# Revit family: Grinder_Pump-Dual_Seal-Zoeller-7011
name_source: partatom
category: Mechanical Equipment
units: mm (PartAtom-declared; Revit-internal decimal feet)

## family parameters
Always vertical = No
Cut with Voids When Loaded = No
OmniClass Number = 23.60.30.21
OmniClass Title = Pumps
Part Type = Normal
Room Calculation Point = No
Round Connector Dimension = Use Radius
Shared = Yes
Work Plane-Based = Yes

## types (1)
- 7011
    Assembly Code = D2010900
    Configuration = Reversing
    Cutter & Plate SS Hardened = 55-60 Rockwell
    Default Elevation = 0"
    Description = Commercial Effluent Pumps
    Discharge Diameter = 1.25" NPT
    Discharge Radius = 5/8"
    Full Load Amps (Voltage Dependent) = 4.5-20.0
    Height = 21 3/32"
    Hertz = 60
    Impeller Diameter = 5 17/32"
    Impeller Trim - Reversing Models Only (Optional) = No
    Impeller Type = Ductile Iron Vortex
    Installation Type = Floor Mounted
    Insulation = Class F
    Lead Wires Insulation = Class F
    Length = 11 19/32"
    Locked Rotor Amps (Voltage Dependant) = 16.2-60.7
    Manufacturer = Zoeller
    Masterformat Number = 33 36 16
    Masterformat Title = Utility Septic Tank Effluent Pumps
    Material = Cast Iron-Zoeller-Powder Coated Epoxy
    Max. Stator Temp. = 311 °F
    Max. Water Temp. = 104 °F
    Maximum KW Input = 3.9
    Model = 7011
    Moisture Sensor (Optional) = Moisture Sensing Probes (Requires a circuit in control panel)
    Motor = 2.0 Pump Name Plate Horsepower
    Motor Design Letter = NEMA B (3 Ph), NEMA L (1 Ph)
    Motor Shaft = 416 S.S.
    Motor Thermal Shutoff = Integral On-Lead (1 PH) or Thermal Cut-Out (3 PH)
    Motor Type = Submersible
    NEC Locked Rotor Code = K
    Nominal Height = 5 3/8"
    O-Rings = Viton
    Omniclass Table 23 Code = 23.60.30.21
    Omniclass Table 23 Title = Pumps
    Operation = Non-Automatic
    Overall Height = 24 7/32"
    Phase = 1 or 3
    Power Cord = 14 Gauge SOW
    Price = Prices may vary. Please consult Manufacturer Representative for most up-to-date price list.
    Product Page URL = http://www.zoellerengprod.com
    RPM = 3450
    Service Factor = 1.2
    Shaft Seal Lower (Options) = Silicon Carbide/Silicon Carbide
    Shaft Seal Lower Standard = Carbon/Silicon Carbide
    Shaft Seal Upper (Options) = Carbon/Silicon Carbide, Silicon Carbide/Silicon Carbide
    Shaft Seal Upper Standard = Carbon/Ceramic
    Shipping Weight = 137 lbs. (1 PH), 132 lbs. (3 PH)
    Tandem Seals = Standard
    Type = Permanent Split Capacitor or 3 Phase
    Type SOW Power Cord Length = 240"
    URL = http://www.zoellerengprod.com
    Voltage = 200-460V
    Warranty Information = 36 Months (Limited)
    Waste Connection = Yes
    Width = 8"

## geometry (parser evidence)
native form markers: Sweep x3
no freeform markers — native parametric forms only
